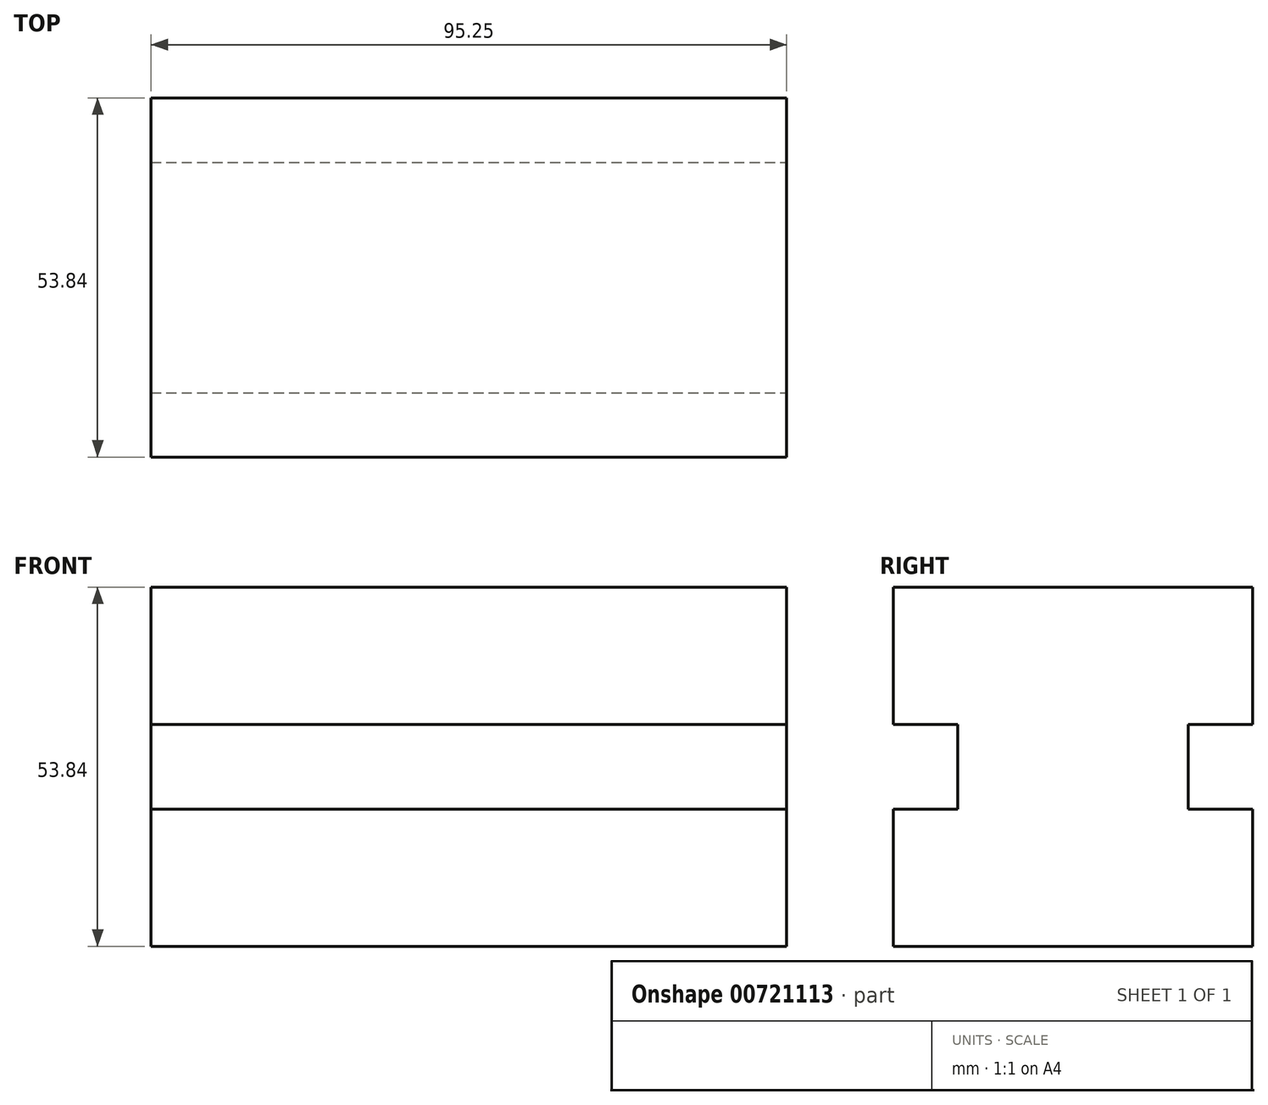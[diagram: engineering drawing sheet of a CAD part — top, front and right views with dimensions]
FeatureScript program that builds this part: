
annotation { "Feature Type Name" : "Feature", "Feature Type Description" : "" }
export const myFeature = defineFeature(function(context is Context, id is Id, definition is map)
    precondition{}
    {
        {
            var Q0;
            Q0=qCreatedBy(makeId("Right.planeOp"),FACE);
            var sketch = newSketch(context, id + "F0", { "sketchPlane" : qUnion([Q0])});
            skLineSegment(sketch, "E0.bottom", {"start": v(-26.92, -26.92) * mm, "end": v(26.92, -26.92) * mm});
            skLineSegment(sketch, "E0.top", {"start": v(-26.92, 26.92) * mm, "end": v(26.92, 26.92) * mm});
            skLineSegment(sketch, "E0.left", {"start": v(-26.92, -26.92) * mm, "end": v(-26.92, -6.35) * mm});
            skLineSegment(sketch, "E0.right", {"start": v(26.92, -26.92) * mm, "end": v(26.92, -6.35) * mm});
            skPoint(sketch, "E0.middle", {"position": v(0, 0) * mm});
            skLineSegment(sketch, "E1.bottom", {"start": v(-26.92, 6.35) * mm, "end": v(-17.27, 6.35) * mm});
            skLineSegment(sketch, "E1.top", {"start": v(-26.92, -6.35) * mm, "end": v(-17.27, -6.35) * mm});
            skLineSegment(sketch, "E1.right", {"start": v(-17.27, 6.35) * mm, "end": v(-17.27, -6.35) * mm});
            skLineSegment(sketch, "E2", {"start": v(0, 37.1) * mm, "end": v(0, -49.2) * mm, "construction": true});
            skPoint(sketch, "E2.startSnap0", {"position": v(0, 26.92) * mm});
            skLineSegment(sketch, "E3.MirrorCS", {"start": v(17.27, 6.35) * mm, "end": v(17.27, -6.35) * mm});
            skLineSegment(sketch, "E4.MirrorCS", {"start": v(26.92, 6.35) * mm, "end": v(17.27, 6.35) * mm});
            skLineSegment(sketch, "E5.MirrorCS", {"start": v(26.92, -6.35) * mm, "end": v(17.27, -6.35) * mm});
            skLineSegment(sketch, "E6.trimOffspring", {"start": v(-26.92, 6.35) * mm, "end": v(-26.92, 26.92) * mm});
            skPoint(sketch, "E7.MirrorCS.end.orphan", {"position": v(26.92, -6.35) * mm});
            skPoint(sketch, "E7.MirrorCS.start.orphan", {"position": v(26.92, 6.35) * mm});
            skLineSegment(sketch, "E8.trimOffspring", {"start": v(26.92, 6.35) * mm, "end": v(26.92, 26.92) * mm});
            skSolve(sketch);
        }
        {
            var Q0;
            Q0=makeQuery(id+"F0.imprint","IMPRINT",FACE,{"disambiguationData":[TD([[makeQuery(id+"F0.imprint","IMPRINT",EDGE,{"derivedFrom":sQuery(id+"F0.wireOp",EDGE,"E0.bottom")}),1.0]])]});
            extrude(context, id + "F1", {"entities" : qUnion([Q0]), "oppositeDirection" : true, "depth" : 95.25 * mm, "offsetDistance" : 25.4 * mm});
        }
    });
